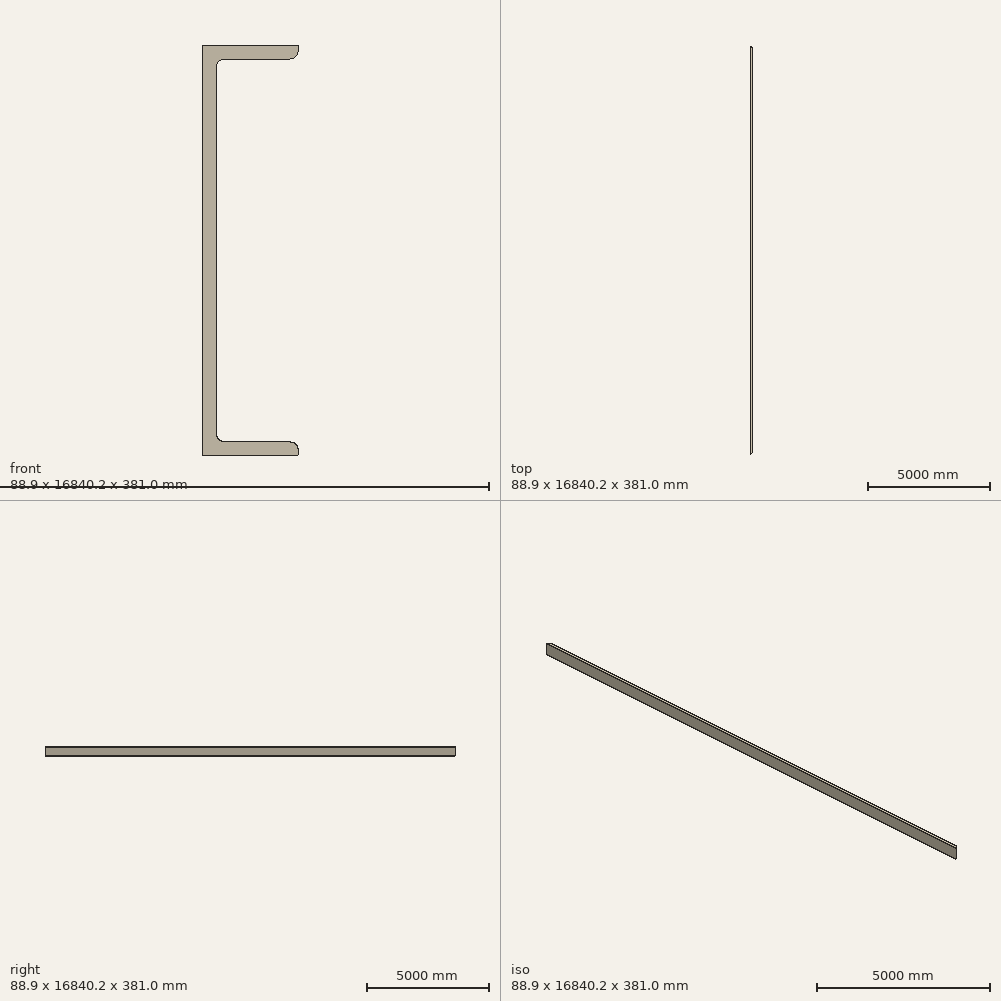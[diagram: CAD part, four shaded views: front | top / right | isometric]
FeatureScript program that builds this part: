
annotation { "Feature Type Name" : "Feature", "Feature Type Description" : "" }
export const myFeature = defineFeature(function(context is Context, id is Id, definition is map)
    precondition{}
    {
        {
            var Q0;
            Q0=qCreatedBy(makeId("Front.planeOp"),FACE);
            var sketch = newSketch(context, id + "F0", { "sketchPlane" : qUnion([Q0])});
            skLineSegment(sketch, "E0", {"start": v(44.45, 190.5) * mm, "end": v(-44.45, 190.5) * mm});
            skLineSegment(sketch, "E1", {"start": v(-44.45, 190.5) * mm, "end": v(-44.45, -190.5) * mm});
            skLineSegment(sketch, "E2", {"start": v(-44.45, -190.5) * mm, "end": v(44.45, -190.5) * mm});
            skLineSegment(sketch, "E3", {"start": v(44.45, -190.5) * mm, "end": v(44.45, -177.8) * mm});
            skLineSegment(sketch, "E4", {"start": v(44.45, -177.8) * mm, "end": v(-31.75, -177.8) * mm});
            skLineSegment(sketch, "E5", {"start": v(-31.75, -177.8) * mm, "end": v(-31.75, 177.8) * mm});
            skLineSegment(sketch, "E6", {"start": v(-31.75, 177.8) * mm, "end": v(44.45, 177.8) * mm});
            skLineSegment(sketch, "E7", {"start": v(44.45, 177.8) * mm, "end": v(44.45, 190.5) * mm});
            skSolve(sketch);
        }
        {
            var Q0;
            Q0=makeQuery(id+"F0.imprint","IMPRINT",FACE,{"disambiguationData":[TD([[makeQuery(id+"F0.imprint","IMPRINT",EDGE,{"derivedFrom":sQuery(id+"F0.wireOp",EDGE,"E0")}),1.0]])]});
            extrude(context, id + "F1", {"entities" : qUnion([Q0]), "depth" : 16764 * mm + 76.2 * mm});
        }
        {
            var Q0;
            Q0=makeQuery(id+"F1.opExtrude","SWEPT_EDGE",EDGE,{"disambiguationData":[OSD([sQuery(id+"F0.wireOp",EDGE,"E3"),sQuery(id+"F0.wireOp",EDGE,"E4")])]});
            var Q1;
            Q1=makeQuery(id+"F1.opExtrude","SWEPT_EDGE",EDGE,{"disambiguationData":[OSD([sQuery(id+"F0.wireOp",EDGE,"E4"),sQuery(id+"F0.wireOp",EDGE,"E5")])]});
            var Q2;
            Q2=makeQuery(id+"F1.opExtrude","SWEPT_EDGE",EDGE,{"disambiguationData":[OSD([sQuery(id+"F0.wireOp",EDGE,"E5"),sQuery(id+"F0.wireOp",EDGE,"E6")])]});
            var Q3;
            Q3=makeQuery(id+"F1.opExtrude","SWEPT_EDGE",EDGE,{"disambiguationData":[OSD([sQuery(id+"F0.wireOp",EDGE,"E6"),sQuery(id+"F0.wireOp",EDGE,"E7")])]});
            fillet(context, id + "F2", {"entities" : qUnion([Q0, Q1, Q2, Q3]), "radius" : 7.62 * mm, "tangentPropagation" : true, "allowEdgeOverflow" : false});
        }
        {
            var Q0;
            Q0=makeQuery(id+"F1.opExtrude","SWEPT_FACE",FACE,{"disambiguationData":[OSD([sQuery(id+"F0.wireOp",EDGE,"E0")])]});
            var sketch = newSketch(context, id + "F3", { "sketchPlane" : qUnion([Q0])});
            skLineSegment(sketch, "E8", {"start": v(-44.45, 0) * mm, "end": v(44.45, -88.9) * mm});
            skLineSegment(sketch, "E9", {"start": v(-44.45, -16840.2) * mm, "end": v(44.45, -16751.3) * mm});
            skSolve(sketch);
        }
        {
            var Q0;
            {var subQ0=sQuery(id+"F3.wireOp",EDGE,"E8");Q0=makeQuery(id+"F3.imprint","IMPRINT",FACE,{"disambiguationData":[TD([[makeQuery(id+"F3.imprint","IMPRINT",EDGE,{"derivedFrom":subQ0}),1.0]])]});}
            extrude(context, id + "F4", {"entities" : qUnion([Q0]), "operationType" : NewBodyOperationType.REMOVE, "endBound" : BoundingType.THROUGH_ALL, "oppositeDirection" : true, "depth" : 25.4 * mm});
        }
        {
            var Q0;
            {var subQ0=sQuery(id+"F3.wireOp",EDGE,"E9");Q0=makeQuery(id+"F3.imprint","IMPRINT",FACE,{"disambiguationData":[TD([[makeQuery(id+"F3.imprint","IMPRINT",EDGE,{"derivedFrom":subQ0}),-1.0]])]});}
            extrude(context, id + "F5", {"entities" : qUnion([Q0]), "operationType" : NewBodyOperationType.REMOVE, "endBound" : BoundingType.THROUGH_ALL, "oppositeDirection" : true, "depth" : 25.4 * mm});
        }
    });
